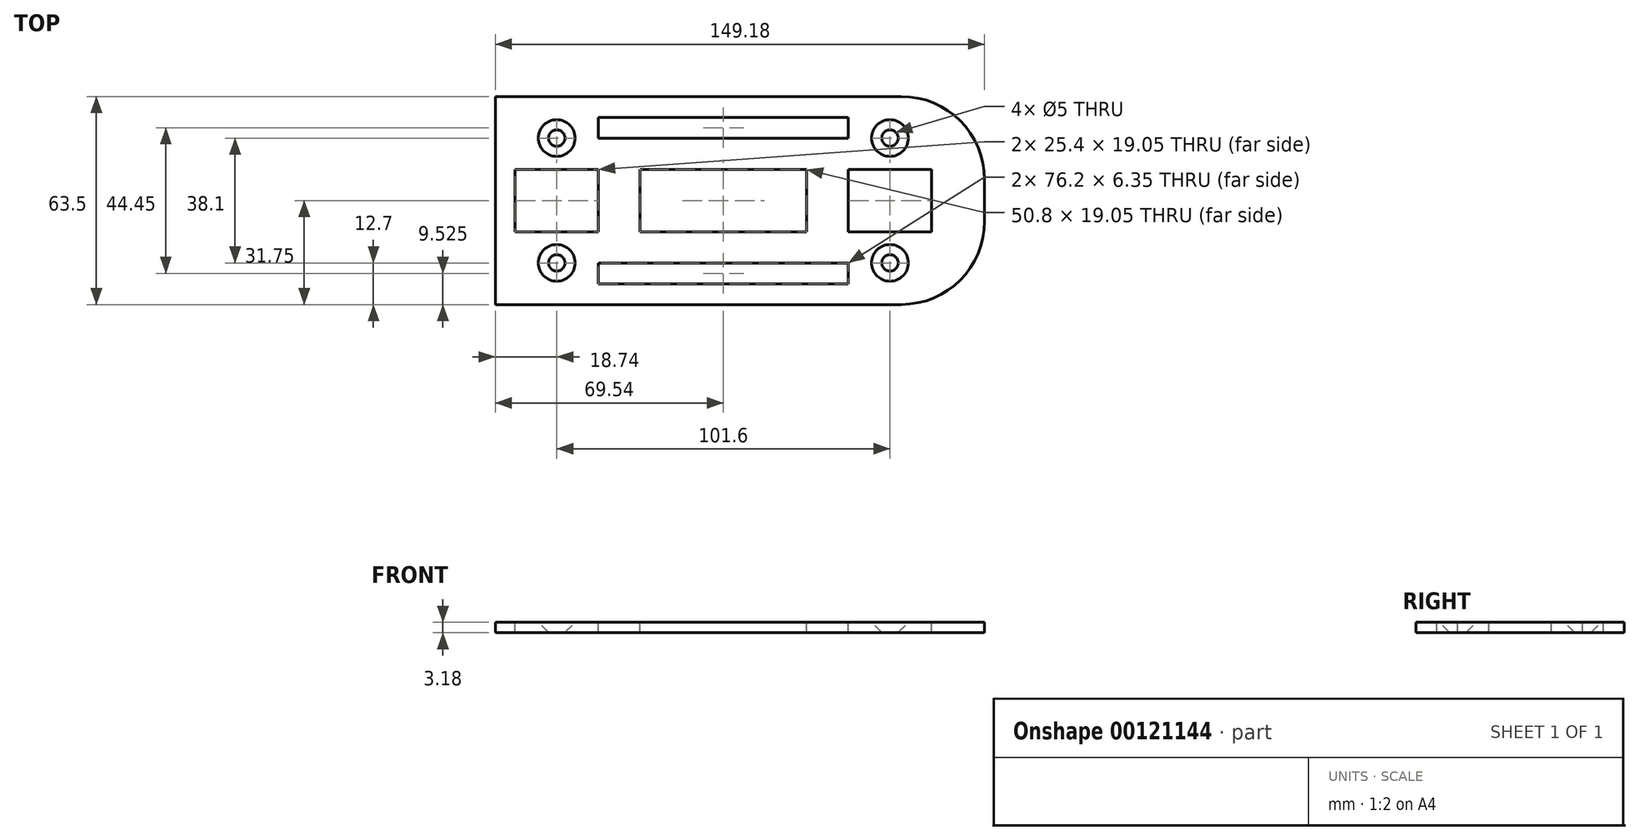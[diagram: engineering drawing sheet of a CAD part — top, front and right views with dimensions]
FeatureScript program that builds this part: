
annotation { "Feature Type Name" : "Feature", "Feature Type Description" : "" }
export const myFeature = defineFeature(function(context is Context, id is Id, definition is map)
    precondition{}
    {
        {
            var Q0;
            Q0=qCreatedBy(makeId("Front.planeOp"),FACE);
            var sketch = newSketch(context, id + "F0", { "sketchPlane" : qUnion([Q0])});
            skPoint(sketch, "E0.middle", {"position": v(0, 0) * mm});
            skLineSegment(sketch, "E1", {"start": v(-82.24, 19.05) * mm, "end": v(66.94, 19.05) * mm});
            skLineSegment(sketch, "E2", {"start": v(-82.24, 19.05) * mm, "end": v(-82.24, -19.05) * mm});
            skFitSpline(sketch, "E3", {"points": [v(-82.24, -19.05) * mm, v(66.94, 19.05) * mm], "startDerivative": vector(246.72, 0) * mm, "endDerivative": vector(0, 114.3) * mm});
            skSolve(sketch);
        }
        {
            var Q0;
            Q0=qSketchRegion(id+"F0",true);
            extrude(context, id + "F1", {"entities" : qUnion([Q0]), "depth" : 31.75 * mm, "hasSecondDirection" : true, "secondDirectionOppositeDirection" : true, "secondDirectionDepth" : 31.75 * mm});
        }
        {
            var Q0;
            Q0=makeQuery(id+"F1.opExtrude","CAP_EDGE",EDGE,{"disambiguationData":[OSD([sQuery(id+"F0.wireOp",EDGE,"E3")])],"isStart":false});
            var Q1;
            Q1=makeQuery(id+"F1.opExtrude","CAP_EDGE",EDGE,{"disambiguationData":[OSD([sQuery(id+"F0.wireOp",EDGE,"E3")])],"isStart":true});
            fillet(context, id + "F2", {"entities" : qUnion([Q0, Q1]), "radius" : 25.4 * mm, "tangentPropagation" : true, "allowEdgeOverflow" : false});
        }
        {
            var Q0;
            Q0=makeQuery(id+"F1.opExtrude","SWEPT_FACE",FACE,{"disambiguationData":[OSD([sQuery(id+"F0.wireOp",EDGE,"E2")])]});
            var sketch = newSketch(context, id + "F3", { "sketchPlane" : qUnion([Q0])});
            skCircle(sketch, "E4", {"center": v(0, 0) * mm, "radius": 6.35 * mm});
            skSolve(sketch);
        }
        {
            var Q0;
            Q0=qSketchRegion(id+"F3",true);
            extrude(context, id + "F4", {"entities" : qUnion([Q0]), "operationType" : NewBodyOperationType.REMOVE, "endBound" : BoundingType.THROUGH_ALL, "oppositeDirection" : true, "depth" : 25.4 * mm});
        }
        {
            var Q0;
            Q0=makeQuery(id+"F1.opExtrude","SWEPT_FACE",FACE,{"disambiguationData":[OSD([sQuery(id+"F0.wireOp",EDGE,"E2")])]});
            var sketch = newSketch(context, id + "F5", { "sketchPlane" : qUnion([Q0])});
            skCircle(sketch, "E5", {"center": v(0, 0) * mm, "radius": 12.7 * mm});
            skSolve(sketch);
        }
        {
            var Q0;
            Q0=qSketchRegion(id+"F5",true);
            extrude(context, id + "F6", {"entities" : qUnion([Q0]), "operationType" : NewBodyOperationType.REMOVE, "oppositeDirection" : true, "depth" : 25.4 * mm});
        }
        {
            var Q0;
            Q0=qCreatedBy(makeId("Right.planeOp"),FACE);
            var sketch = newSketch(context, id + "F7", { "sketchPlane" : qUnion([Q0])});
            skCircle(sketch, "E6", {"center": v(0, 0) * mm, "radius": 9.53 * mm});
            skSolve(sketch);
        }
        {
            var Q0;
            Q0=qSketchRegion(id+"F7",true);
            extrude(context, id + "F8", {"entities" : qUnion([Q0]), "operationType" : NewBodyOperationType.REMOVE, "oppositeDirection" : true, "depth" : 44.45 * mm, "hasSecondDirection" : true, "secondDirectionBound" : SecondDirectionBoundingType.THROUGH_ALL, "secondDirectionOppositeDirection" : false, "secondDirectionDepth" : 25.4 * mm});
        }
        {
            var Q0;
            Q0=makeQuery(id+"F1.opExtrude","SWEPT_FACE",FACE,{"disambiguationData":[OSD([sQuery(id+"F0.wireOp",EDGE,"E1")])]});
            var sketch = newSketch(context, id + "F9", { "sketchPlane" : qUnion([Q0])});
            skPoint(sketch, "E7", {"position": v(-63.5, 19.05) * mm});
            skPoint(sketch, "E8", {"position": v(-63.5, -19.05) * mm});
            skPoint(sketch, "E9", {"position": v(25.4, -19.05) * mm});
            skPoint(sketch, "E10", {"position": v(25.4, 19.05) * mm});
            skSolve(sketch);
        }
        {
            var Q0;
            Q0=sQuery(id+"F9.wireOp",VERTEX,"E7");
            var Q1;
            Q1=sQuery(id+"F9.wireOp",VERTEX,"E8");
            var Q2;
            Q2=sQuery(id+"F9.wireOp",VERTEX,"E10");
            var Q3;
            Q3=sQuery(id+"F9.wireOp",VERTEX,"E9");
            var Q4;
            Q4=makeQuery(id+"F1.opExtrude","SWEPT_BODY",BODY,{"disambiguationData":[OSD([sQuery(id+"F0.wireOp",EDGE,"E1"),sQuery(id+"F0.wireOp",EDGE,"E2"),sQuery(id+"F0.wireOp",EDGE,"E3")])]});
            hole(context, id + "F10", {"style" : HoleStyle.SIMPLE, "endStyle" : HoleEndStyle.BLIND, "standardTappedOrClearance" : lookupTablePath({ "standard" : "ISO", "engagement" : "75%", "pitch" : "0.8 mm", "size" : "M5", "type" : "Tapped" }), "standardBlindInLast" : lookupTablePath({ "standard" : "ISO", "engagement" : "75%", "pitch" : "0.8 mm", "size" : "M5", "type" : "Tapped" }), "holeDiameter" : 4.2 * mm, "holeDepth" : 25.4 * mm, "startFromSketch" : true, "locations" : qUnion([Q0, Q1, Q2, Q3]), "scope" : qUnion([Q4]), "majorDiameter" : 5 * mm});
        }
        {
            var Q0;
            Q0=makeQuery(id+"F1.opExtrude","SWEPT_FACE",FACE,{"disambiguationData":[OSD([sQuery(id+"F0.wireOp",EDGE,"E1")])]});
            var sketch = newSketch(context, id + "F11", { "sketchPlane" : qUnion([Q0])});
            skLineSegment(sketch, "E11.bottom", {"start": v(-82.24, 31.75) * mm, "end": v(41.54, 31.75) * mm});
            skLineSegment(sketch, "E11.top", {"start": v(-82.24, -31.75) * mm, "end": v(41.54, -31.75) * mm});
            skLineSegment(sketch, "E11.left", {"start": v(-82.24, 31.75) * mm, "end": v(-82.24, -31.75) * mm});
            skLineSegment(sketch, "E12", {"start": v(66.94, 6.35) * mm, "end": v(66.94, -6.35) * mm});
            skArc(sketch, "E13.0", {"start": v(66.94, 6.35) * mm, "mid": v(59.5, 24.31) * mm, "end": v(41.54, 31.75) * mm});
            skArc(sketch, "E14.0", {"start": v(41.54, -31.75) * mm, "mid": v(59.5, -24.31) * mm, "end": v(66.94, -6.35) * mm});
            skSolve(sketch);
        }
        {
            var Q0;
            Q0=qSketchRegion(id+"F11",true);
            extrude(context, id + "F12", {"entities" : qUnion([Q0]), "depth" : 3.17 * mm});
        }
        {
            var Q0;
            Q0=makeQuery(id+"F12.opExtrude","CAP_FACE",FACE,{"disambiguationData":[OSD([sQuery(id+"F11.wireOp",EDGE,"E11.bottom"),sQuery(id+"F11.wireOp",EDGE,"E11.top"),sQuery(id+"F11.wireOp",EDGE,"E11.left"),sQuery(id+"F11.wireOp",EDGE,"E12"),sQuery(id+"F11.wireOp",EDGE,"E13.0"),sQuery(id+"F11.wireOp",EDGE,"E14.0")])],"isStart":false});
            var sketch = newSketch(context, id + "F13", { "sketchPlane" : qUnion([Q0])});
            skPoint(sketch, "E15", {"position": v(-63.5, 19.05) * mm});
            skPoint(sketch, "E16", {"position": v(-63.5, -19.05) * mm});
            skPoint(sketch, "E17", {"position": v(38.1, -19.05) * mm});
            skPoint(sketch, "E18", {"position": v(38.1, 19.05) * mm});
            skSolve(sketch);
        }
        {
            var Q0;
            Q0=sQuery(id+"F13.wireOp",VERTEX,"E15");
            var Q1;
            Q1=sQuery(id+"F13.wireOp",VERTEX,"E16");
            var Q2;
            Q2=sQuery(id+"F13.wireOp",VERTEX,"E17");
            var Q3;
            Q3=sQuery(id+"F13.wireOp",VERTEX,"E18");
            var Q4;
            Q4=makeQuery(id+"F12.opExtrude","SWEPT_BODY",BODY,{"disambiguationData":[OSD([sQuery(id+"F11.wireOp",EDGE,"E11.bottom"),sQuery(id+"F11.wireOp",EDGE,"E11.top"),sQuery(id+"F11.wireOp",EDGE,"E11.left"),sQuery(id+"F11.wireOp",EDGE,"E12"),sQuery(id+"F11.wireOp",EDGE,"E13.0"),sQuery(id+"F11.wireOp",EDGE,"E14.0")])]});
            hole(context, id + "F14", {"style" : HoleStyle.C_SINK, "endStyle" : HoleEndStyle.THROUGH, "standardTappedOrClearance" : lookupTablePath({ "standard" : "ISO", "size" : "5", "type" : "Drilled" }), "standardBlindInLast" : lookupTablePath({ "standard" : "ISO", "size" : "5", "type" : "Drilled" }), "holeDiameter" : 5 * mm, "cSinkDiameter" : 11.2 * mm, "cSinkAngle" : 90 * degree, "startFromSketch" : true, "locations" : qUnion([Q0, Q1, Q2, Q3]), "scope" : qUnion([Q4]), "isTappedThrough" : true});
        }
        {
            var Q0;
            Q0=makeQuery(id+"F12.opExtrude","CAP_FACE",FACE,{"disambiguationData":[OSD([sQuery(id+"F11.wireOp",EDGE,"E11.bottom"),sQuery(id+"F11.wireOp",EDGE,"E11.top"),sQuery(id+"F11.wireOp",EDGE,"E11.left"),sQuery(id+"F11.wireOp",EDGE,"E12"),sQuery(id+"F11.wireOp",EDGE,"E13.0"),sQuery(id+"F11.wireOp",EDGE,"E14.0")])],"isStart":false});
            var sketch = newSketch(context, id + "F15", { "sketchPlane" : qUnion([Q0])});
            skLineSegment(sketch, "E19.left", {"start": v(-76.2, 9.52) * mm, "end": v(-76.2, -9.53) * mm});
            skLineSegment(sketch, "E19.right", {"start": v(50.8, 9.53) * mm, "end": v(50.8, -9.52) * mm});
            skLineSegment(sketch, "E20.bottom", {"start": v(-50.8, 25.4) * mm, "end": v(25.4, 25.4) * mm});
            skLineSegment(sketch, "E20.top", {"start": v(-50.8, 19.05) * mm, "end": v(25.4, 19.05) * mm});
            skLineSegment(sketch, "E20.left", {"start": v(-50.8, 25.4) * mm, "end": v(-50.8, 19.05) * mm});
            skLineSegment(sketch, "E20.right", {"start": v(25.4, 25.4) * mm, "end": v(25.4, 19.05) * mm});
            skLineSegment(sketch, "E21.bottom", {"start": v(-50.8, -19.05) * mm, "end": v(25.4, -19.05) * mm});
            skLineSegment(sketch, "E21.top", {"start": v(-50.8, -25.4) * mm, "end": v(25.4, -25.4) * mm});
            skLineSegment(sketch, "E21.left", {"start": v(-50.8, -19.05) * mm, "end": v(-50.8, -25.4) * mm});
            skLineSegment(sketch, "E21.right", {"start": v(25.4, -19.05) * mm, "end": v(25.4, -25.4) * mm});
            skLineSegment(sketch, "E22", {"start": v(-50.8, 9.52) * mm, "end": v(-50.8, -9.52) * mm});
            skLineSegment(sketch, "E23", {"start": v(25.4, 9.53) * mm, "end": v(25.4, -9.52) * mm});
            skLineSegment(sketch, "E24", {"start": v(-38.1, 9.52) * mm, "end": v(-38.1, -9.52) * mm});
            skLineSegment(sketch, "E25", {"start": v(12.7, 9.53) * mm, "end": v(12.7, -9.52) * mm});
            skLineSegment(sketch, "E26", {"start": v(-76.2, 9.52) * mm, "end": v(-50.8, 9.52) * mm});
            skLineSegment(sketch, "E27", {"start": v(-38.1, 9.52) * mm, "end": v(12.7, 9.53) * mm});
            skLineSegment(sketch, "E28", {"start": v(25.4, 9.53) * mm, "end": v(50.8, 9.53) * mm});
            skLineSegment(sketch, "E29", {"start": v(-76.2, -9.53) * mm, "end": v(-50.8, -9.52) * mm});
            skLineSegment(sketch, "E30", {"start": v(-38.1, -9.52) * mm, "end": v(12.7, -9.52) * mm});
            skLineSegment(sketch, "E31", {"start": v(25.4, -9.52) * mm, "end": v(50.8, -9.52) * mm});
            skSolve(sketch);
        }
        {
            var Q0;
            Q0 = qSketchRegion(id + "F15", true);
            extrude(context, id + "F16", {"entities" : qUnion([Q0]), "operationType" : NewBodyOperationType.REMOVE, "endBound" : BoundingType.THROUGH_ALL, "oppositeDirection" : true, "depth" : 25.4 * mm});
        }
        {
            var Q0;
            Q0=makeQuery(id+"F1.opExtrude","SWEPT_BODY",BODY,{"disambiguationData":[OSD([sQuery(id+"F0.wireOp",EDGE,"E1"),sQuery(id+"F0.wireOp",EDGE,"E2"),sQuery(id+"F0.wireOp",EDGE,"E3")])]});
            deleteBodies(context, id + "F17", {"entities" : qUnion([Q0])});
        }
    });
